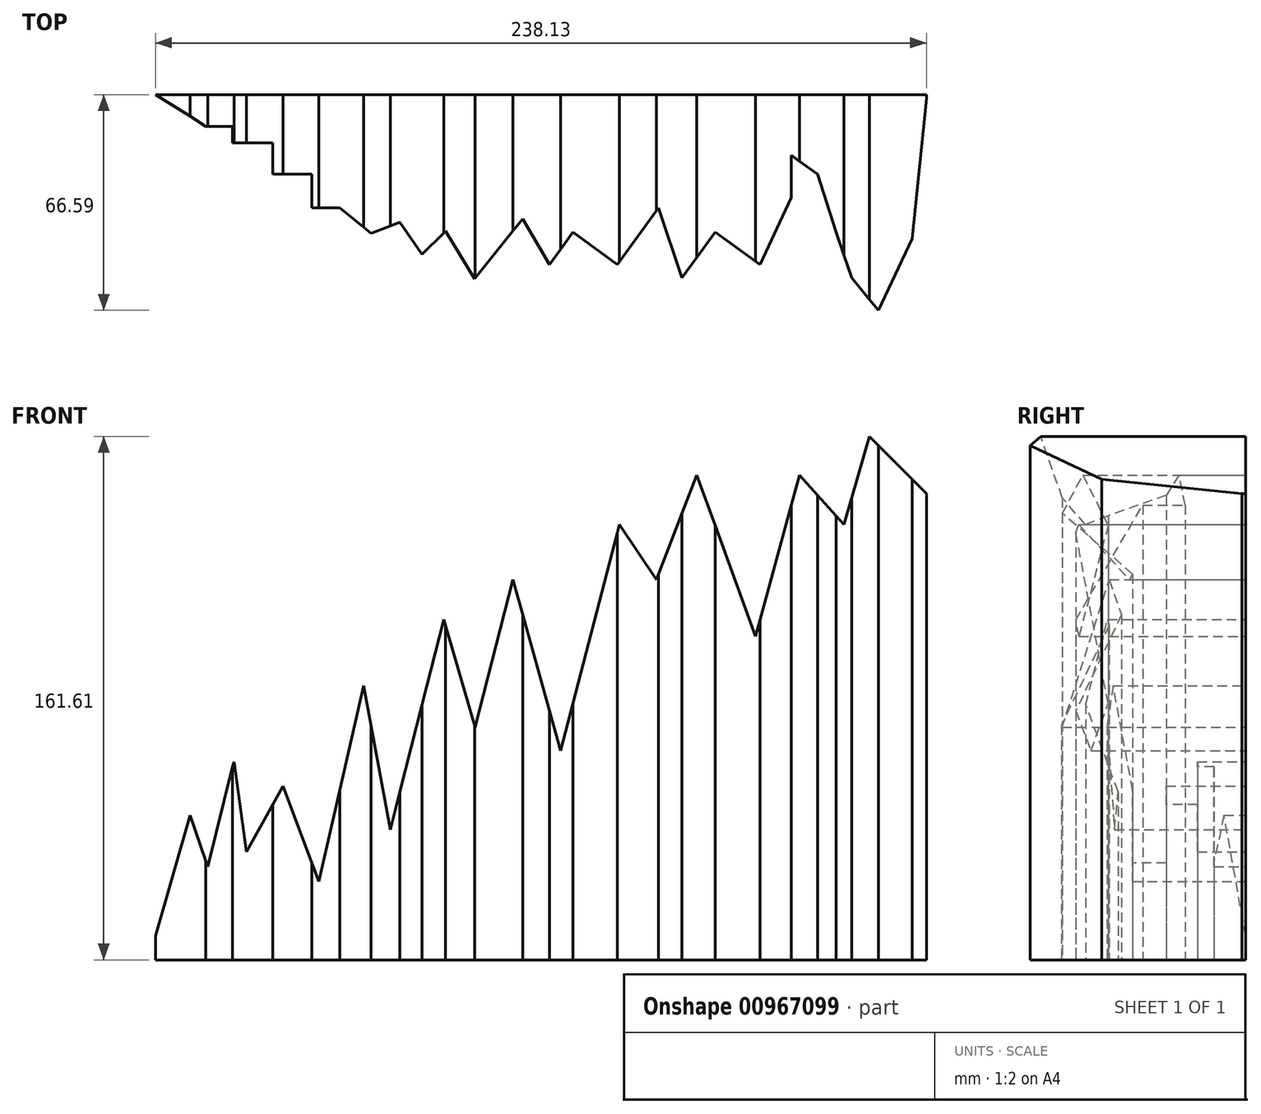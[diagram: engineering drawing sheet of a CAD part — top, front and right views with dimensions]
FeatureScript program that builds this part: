
annotation { "Feature Type Name" : "Feature", "Feature Type Description" : "" }
export const myFeature = defineFeature(function(context is Context, id is Id, definition is map)
    precondition{}
    {
        {
            var Q0;
            Q0=qCreatedBy(makeId("Front.planeOp"),FACE);
            var sketch = newSketch(context, id + "F0", { "sketchPlane" : qUnion([Q0])});
            skLineSegment(sketch, "E0", {"start": v(0, 7.38) * mm, "end": v(10.66, 44.64) * mm});
            skLineSegment(sketch, "E1", {"start": v(10.66, 44.64) * mm, "end": v(16.18, 28.77) * mm});
            skLineSegment(sketch, "E2", {"start": v(16.18, 28.77) * mm, "end": v(24.23, 61.2) * mm});
            skLineSegment(sketch, "E3", {"start": v(24.23, 61.2) * mm, "end": v(28.14, 33.37) * mm});
            skLineSegment(sketch, "E4", {"start": v(28.14, 33.37) * mm, "end": v(39.41, 53.61) * mm});
            skLineSegment(sketch, "E5", {"start": v(39.41, 53.61) * mm, "end": v(50.45, 24.17) * mm});
            skLineSegment(sketch, "E6", {"start": v(50.45, 24.17) * mm, "end": v(64.25, 84.66) * mm});
            skLineSegment(sketch, "E7", {"start": v(64.25, 84.66) * mm, "end": v(72.53, 40.27) * mm});
            skLineSegment(sketch, "E8", {"start": v(72.53, 40.27) * mm, "end": v(89.1, 105.13) * mm});
            skLineSegment(sketch, "E9", {"start": v(89.1, 105.13) * mm, "end": v(98.75, 71.78) * mm});
            skLineSegment(sketch, "E10", {"start": v(98.75, 71.78) * mm, "end": v(110.39, 117.36) * mm});
            skLineSegment(sketch, "E11", {"start": v(110.39, 117.36) * mm, "end": v(125.08, 64.57) * mm});
            skLineSegment(sketch, "E12", {"start": v(125.08, 64.57) * mm, "end": v(143.34, 134.43) * mm});
            skLineSegment(sketch, "E13", {"start": v(143.34, 134.43) * mm, "end": v(154.72, 117.36) * mm});
            skLineSegment(sketch, "E14", {"start": v(154.72, 117.36) * mm, "end": v(167.22, 149.71) * mm});
            skLineSegment(sketch, "E15", {"start": v(167.22, 149.71) * mm, "end": v(185.28, 99.94) * mm});
            skLineSegment(sketch, "E16", {"start": v(185.28, 99.94) * mm, "end": v(198.93, 149.71) * mm});
            skLineSegment(sketch, "E17", {"start": v(198.93, 149.71) * mm, "end": v(212.59, 134.43) * mm});
            skLineSegment(sketch, "E18", {"start": v(212.59, 134.43) * mm, "end": v(220.51, 161.6) * mm});
            skLineSegment(sketch, "E19", {"start": v(220.51, 161.6) * mm, "end": v(238.13, 143.99) * mm});
            skLineSegment(sketch, "E20", {"start": v(238.13, 143.99) * mm, "end": v(238.13, 0) * mm});
            skLineSegment(sketch, "E21", {"start": v(238.13, 0) * mm, "end": v(0, 0) * mm});
            skLineSegment(sketch, "E22", {"start": v(0, 0) * mm, "end": v(0, 7.38) * mm});
            skSolve(sketch);
        }
        {
            var Q0;
            Q0=qCreatedBy(makeId("Top.planeOp"),FACE);
            var sketch = newSketch(context, id + "F1", { "sketchPlane" : qUnion([Q0])});
            skLineSegment(sketch, "E23", {"start": v(0, 0) * mm, "end": v(15.57, -9.76) * mm});
            skLineSegment(sketch, "E24", {"start": v(15.57, -9.76) * mm, "end": v(23.83, -9.76) * mm});
            skLineSegment(sketch, "E25", {"start": v(23.83, -9.76) * mm, "end": v(23.83, -14.93) * mm});
            skLineSegment(sketch, "E26", {"start": v(23.83, -14.93) * mm, "end": v(36.23, -14.93) * mm});
            skLineSegment(sketch, "E27", {"start": v(36.23, -14.93) * mm, "end": v(36.23, -24.57) * mm});
            skLineSegment(sketch, "E28", {"start": v(36.23, -24.57) * mm, "end": v(48.29, -24.57) * mm});
            skLineSegment(sketch, "E29", {"start": v(48.29, -24.57) * mm, "end": v(48.29, -34.9) * mm});
            skLineSegment(sketch, "E30", {"start": v(48.29, -34.9) * mm, "end": v(56.9, -34.9) * mm});
            skLineSegment(sketch, "E31", {"start": v(56.9, -34.9) * mm, "end": v(66.54, -42.83) * mm});
            skLineSegment(sketch, "E32", {"start": v(66.54, -42.83) * mm, "end": v(75.5, -39.38) * mm});
            skLineSegment(sketch, "E33", {"start": v(75.5, -39.38) * mm, "end": v(82.39, -49.37) * mm});
            skLineSegment(sketch, "E34", {"start": v(82.39, -49.37) * mm, "end": v(89.62, -42.14) * mm});
            skLineSegment(sketch, "E35", {"start": v(89.62, -42.14) * mm, "end": v(98.58, -56.95) * mm});
            skLineSegment(sketch, "E36", {"start": v(98.58, -56.95) * mm, "end": v(113.39, -38.35) * mm});
            skLineSegment(sketch, "E37", {"start": v(113.39, -38.35) * mm, "end": v(121.65, -52.47) * mm});
            skLineSegment(sketch, "E38", {"start": v(121.65, -52.47) * mm, "end": v(128.89, -42.48) * mm});
            skLineSegment(sketch, "E39", {"start": v(128.89, -42.48) * mm, "end": v(142.68, -52.47) * mm});
            skLineSegment(sketch, "E40", {"start": v(142.68, -52.47) * mm, "end": v(155.4, -34.9) * mm});
            skLineSegment(sketch, "E41", {"start": v(155.4, -34.9) * mm, "end": v(162.64, -56.6) * mm});
            skLineSegment(sketch, "E42", {"start": v(162.64, -56.6) * mm, "end": v(172.87, -42.48) * mm});
            skLineSegment(sketch, "E43", {"start": v(172.87, -42.48) * mm, "end": v(186.66, -52.47) * mm});
            skLineSegment(sketch, "E44", {"start": v(186.66, -52.47) * mm, "end": v(196.4, -31.8) * mm});
            skLineSegment(sketch, "E45", {"start": v(196.4, -31.8) * mm, "end": v(196.4, -18.72) * mm});
            skLineSegment(sketch, "E46", {"start": v(196.4, -18.72) * mm, "end": v(204.48, -24.57) * mm});
            skLineSegment(sketch, "E47", {"start": v(204.48, -24.57) * mm, "end": v(210.17, -42.48) * mm});
            skLineSegment(sketch, "E48", {"start": v(210.17, -42.48) * mm, "end": v(215, -56.6) * mm});
            skLineSegment(sketch, "E49", {"start": v(215, -56.6) * mm, "end": v(223.26, -66.6) * mm});
            skLineSegment(sketch, "E50", {"start": v(223.26, -66.6) * mm, "end": v(233.68, -44.47) * mm});
            skLineSegment(sketch, "E51", {"start": v(233.68, -44.47) * mm, "end": v(238.25, 0) * mm});
            skLineSegment(sketch, "E52", {"start": v(238.25, 0) * mm, "end": v(0, 0) * mm});
            skSolve(sketch);
        }
        {
            var Q0;
            Q0 = qSketchRegion(id + "F1", true);
            extrude(context, id + "F2", {"entities" : qUnion([Q0]), "depth" : 188.47 * mm, "offsetDistance" : 25.4 * mm});
        }
        {
            var Q0;
            Q0 = qSketchRegion(id + "F0", true);
            extrude(context, id + "F3", {"entities" : qUnion([Q0]), "operationType" : NewBodyOperationType.INTERSECT, "endBound" : BoundingType.THROUGH_ALL, "depth" : 25.4 * mm, "offsetDistance" : 25.4 * mm});
        }
    });
